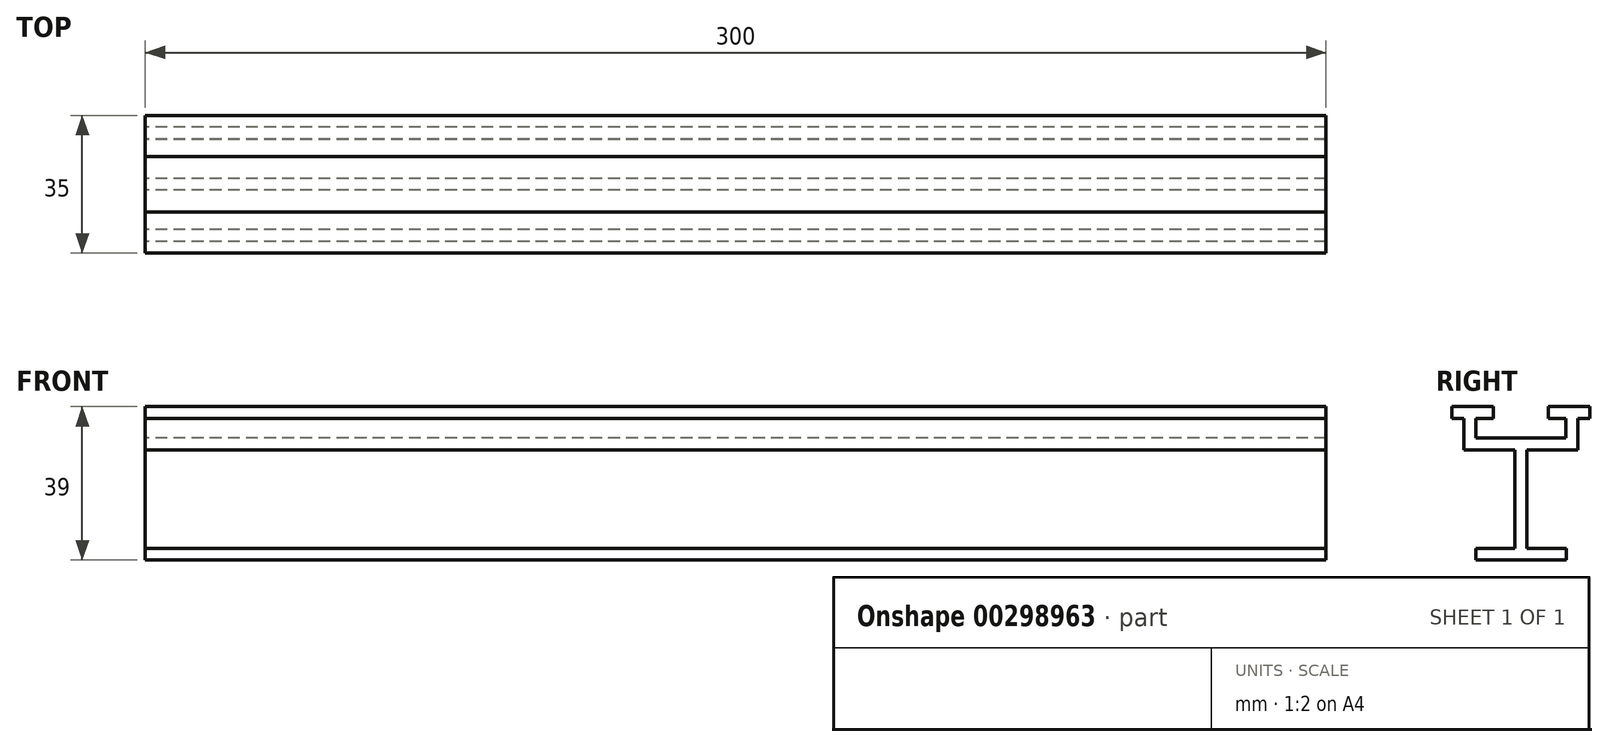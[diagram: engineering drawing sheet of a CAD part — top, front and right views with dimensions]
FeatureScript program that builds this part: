
annotation { "Feature Type Name" : "Feature", "Feature Type Description" : "" }
export const myFeature = defineFeature(function(context is Context, id is Id, definition is map)
    precondition{}
    {
        {
            var Q0;
            Q0=qCreatedBy(makeId("Right.planeOp"),FACE);
            var sketch = newSketch(context, id + "F0", { "sketchPlane" : qUnion([Q0])});
            skLineSegment(sketch, "E0.top", {"start": v(11.5, -1.5) * mm, "end": v(-11.5, -1.5) * mm});
            skLineSegment(sketch, "E0.left", {"start": v(11.5, 1.5) * mm, "end": v(11.5, -1.5) * mm});
            skLineSegment(sketch, "E0.right", {"start": v(-11.5, 1.5) * mm, "end": v(-11.5, -1.5) * mm});
            skPoint(sketch, "E0.middle", {"position": v(0, 0) * mm});
            skLineSegment(sketch, "E1.left", {"start": v(1.5, 26.5) * mm, "end": v(1.5, 1.5) * mm});
            skLineSegment(sketch, "E1.right", {"start": v(-1.5, 26.5) * mm, "end": v(-1.5, 1.5) * mm});
            skPoint(sketch, "E1.middle", {"position": v(0, 14) * mm});
            skLineSegment(sketch, "E2.left", {"start": v(14.5, 26.5) * mm, "end": v(14.5, 29.5) * mm});
            skLineSegment(sketch, "E2.right", {"start": v(-14.5, 26.5) * mm, "end": v(-14.5, 29.5) * mm});
            skPoint(sketch, "E2.middle", {"position": v(0, 28) * mm});
            skLineSegment(sketch, "E3", {"start": v(14.5, 29.5) * mm, "end": v(14.5, 34.5) * mm});
            skLineSegment(sketch, "E4", {"start": v(14.5, 34.5) * mm, "end": v(17.5, 34.5) * mm});
            skLineSegment(sketch, "E5", {"start": v(17.5, 34.5) * mm, "end": v(17.5, 37.5) * mm});
            skLineSegment(sketch, "E6", {"start": v(17.5, 37.5) * mm, "end": v(11.4, 37.5) * mm});
            skLineSegment(sketch, "E7", {"start": v(11.4, 29.5) * mm, "end": v(-11.46, 29.5) * mm});
            skLineSegment(sketch, "E8", {"start": v(-14.5, 34.5) * mm, "end": v(-14.5, 29.5) * mm});
            skLineSegment(sketch, "E9", {"start": v(-11.5, 1.5) * mm, "end": v(-1.5, 1.5) * mm});
            skLineSegment(sketch, "E10", {"start": v(-1.5, 26.5) * mm, "end": v(-14.5, 26.5) * mm});
            skLineSegment(sketch, "E11", {"start": v(1.5, 26.5) * mm, "end": v(14.5, 26.5) * mm});
            skLineSegment(sketch, "E12", {"start": v(1.5, 1.5) * mm, "end": v(11.5, 1.5) * mm});
            skLineSegment(sketch, "E13", {"start": v(-11.46, 37.5) * mm, "end": v(-7, 37.5) * mm});
            skLineSegment(sketch, "E14", {"start": v(-7, 37.5) * mm, "end": v(-7, 34.5) * mm});
            skLineSegment(sketch, "E15", {"start": v(-7, 34.5) * mm, "end": v(-11.46, 34.5) * mm});
            skLineSegment(sketch, "E16", {"start": v(11.4, 37.5) * mm, "end": v(7, 37.5) * mm});
            skLineSegment(sketch, "E17", {"start": v(7, 37.5) * mm, "end": v(7, 34.5) * mm});
            skLineSegment(sketch, "E18", {"start": v(7, 34.5) * mm, "end": v(11.4, 34.5) * mm});
            skLineSegment(sketch, "E19", {"start": v(-11.46, 29.5) * mm, "end": v(-11.46, 34.5) * mm});
            skLineSegment(sketch, "E20", {"start": v(11.4, 29.5) * mm, "end": v(11.4, 34.5) * mm});
            skLineSegment(sketch, "E21.MirrorCS", {"start": v(-17.5, 34.5) * mm, "end": v(-17.5, 37.5) * mm});
            skLineSegment(sketch, "E22.MirrorCS", {"start": v(-17.5, 37.5) * mm, "end": v(-11.4, 37.5) * mm});
            skLineSegment(sketch, "E23.MirrorCS", {"start": v(-14.5, 34.5) * mm, "end": v(-17.5, 34.5) * mm});
            skSolve(sketch);
        }
        {
            var Q0;
            Q0=makeQuery(id+"F0.imprint","IMPRINT",FACE,{"disambiguationData":[TD([[makeQuery(id+"F0.imprint","IMPRINT",EDGE,{"derivedFrom":sQuery(id+"F0.wireOp",EDGE,"E0.top")}),-1.0]])]});
            extrude(context, id + "F1", {"entities" : qUnion([Q0]), "depth" : 150 * mm, "hasSecondDirection" : true, "secondDirectionOppositeDirection" : true, "secondDirectionDepth" : 150 * mm});
        }
    });
